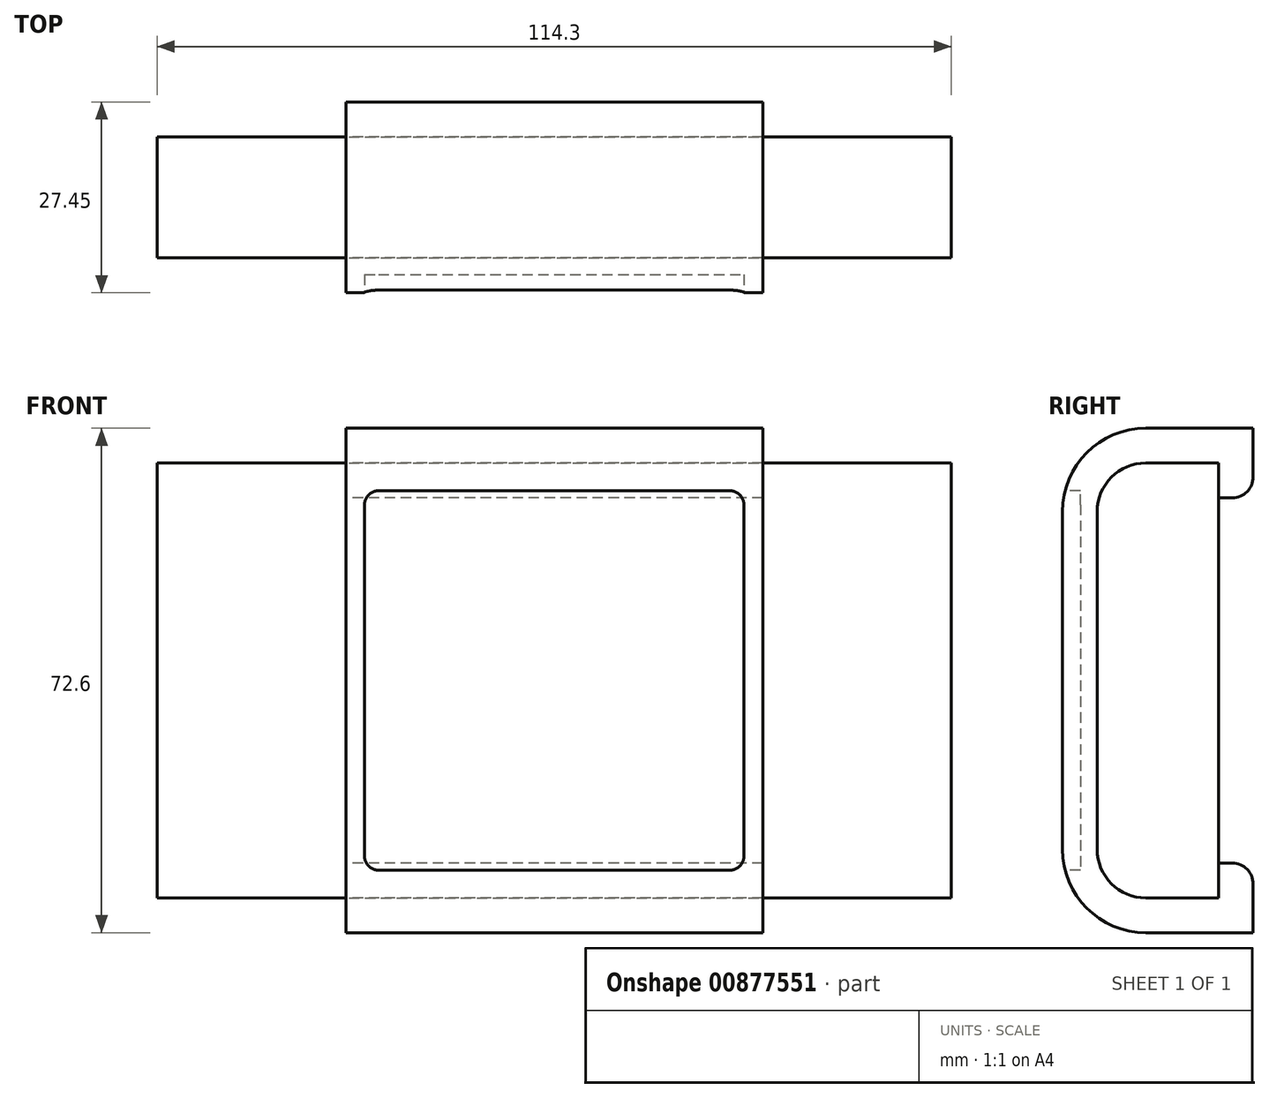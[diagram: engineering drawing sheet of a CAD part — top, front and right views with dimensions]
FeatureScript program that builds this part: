
annotation { "Feature Type Name" : "Feature", "Feature Type Description" : "" }
export const myFeature = defineFeature(function(context is Context, id is Id, definition is map)
    precondition{}
    {
        {
            var Q0;
            Q0=qCreatedBy(makeId("Front.planeOp"),FACE);
            var sketch = newSketch(context, id + "F0", { "sketchPlane" : qUnion([Q0])});
            skLineSegment(sketch, "E0.bottom", {"start": v(-57.15, 31.3) * mm, "end": v(57.15, 31.3) * mm});
            skLineSegment(sketch, "E0.top", {"start": v(-57.15, -31.3) * mm, "end": v(57.15, -31.3) * mm});
            skLineSegment(sketch, "E0.left", {"start": v(-57.15, 31.3) * mm, "end": v(-57.15, -31.3) * mm});
            skLineSegment(sketch, "E0.right", {"start": v(57.15, 31.3) * mm, "end": v(57.15, -31.3) * mm});
            skLineSegment(sketch, "E1", {"start": v(57.15, 31.3) * mm, "end": v(-57.15, -31.3) * mm, "construction": true});
            skLineSegment(sketch, "E2", {"start": v(-57.15, 31.3) * mm, "end": v(57.15, -31.3) * mm, "construction": true});
            skSolve(sketch);
        }
        {
            var Q0;
            Q0=makeQuery(id+"F0.imprint","IMPRINT",FACE,{"disambiguationData":[TD([[makeQuery(id+"F0.imprint","IMPRINT",EDGE,{"derivedFrom":sQuery(id+"F0.wireOp",EDGE,"E0.bottom")}),-1.0]])]});
            extrude(context, id + "F1", {"entities" : qUnion([Q0]), "depth" : 17.45 * mm, "offsetDistance" : 25 * mm});
        }
        {
            var Q0;
            Q0=makeQuery(id+"F1.opExtrude","CAP_EDGE",EDGE,{"disambiguationData":[OSD([sQuery(id+"F0.wireOp",EDGE,"E0.bottom")])],"isStart":false});
            var Q1;
            Q1=makeQuery(id+"F1.opExtrude","CAP_EDGE",EDGE,{"disambiguationData":[OSD([sQuery(id+"F0.wireOp",EDGE,"E0.top")])],"isStart":false});
            fillet(context, id + "F2", {"entities" : qUnion([Q0, Q1]), "radius" : 7 * mm, "tangentPropagation" : true, "allowEdgeOverflow" : false});
        }
        {
            var Q0;
            Q0=qCreatedBy(makeId("Right.planeOp"),FACE);
            var sketch = newSketch(context, id + "F3", { "sketchPlane" : qUnion([Q0])});
            skArc(sketch, "E3.0", {"start": v(-10.45, 36.3) * mm, "mid": v(-18.94, 32.79) * mm, "end": v(-22.45, 24.3) * mm});
            skArc(sketch, "E3.1", {"start": v(-22.45, -24.3) * mm, "mid": v(-18.94, -32.79) * mm, "end": v(-10.45, -36.3) * mm});
            skLineSegment(sketch, "E3.2", {"start": v(-10.45, -36.3) * mm, "end": v(5, -36.3) * mm});
            skLineSegment(sketch, "E3.3", {"start": v(-22.45, 24.3) * mm, "end": v(-22.45, -24.3) * mm});
            skLineSegment(sketch, "E3.4", {"start": v(5, -36.3) * mm, "end": v(5, -26.3) * mm});
            skLineSegment(sketch, "E3.5", {"start": v(5, 36.3) * mm, "end": v(-10.45, 36.3) * mm});
            skLineSegment(sketch, "E4", {"start": v(5, 26.3) * mm, "end": v(0, 26.3) * mm});
            skLineSegment(sketch, "E5", {"start": v(0, -26.3) * mm, "end": v(5, -26.3) * mm});
            skLineSegment(sketch, "E6.trimOffspring", {"start": v(5, 26.3) * mm, "end": v(5, 36.3) * mm});
            skLineSegment(sketch, "E7.0", {"start": v(0, -31.3) * mm, "end": v(0, -26.3) * mm});
            skLineSegment(sketch, "E7.1", {"start": v(-10.45, -31.3) * mm, "end": v(0, -31.3) * mm});
            skArc(sketch, "E7.2", {"start": v(-17.45, -24.3) * mm, "mid": v(-15.4, -29.25) * mm, "end": v(-10.45, -31.3) * mm});
            skLineSegment(sketch, "E7.3", {"start": v(0, 26.3) * mm, "end": v(0, 31.3) * mm});
            skLineSegment(sketch, "E7.4", {"start": v(0, 31.3) * mm, "end": v(-10.45, 31.3) * mm});
            skArc(sketch, "E7.5", {"start": v(-10.45, 31.3) * mm, "mid": v(-15.4, 29.25) * mm, "end": v(-17.45, 24.3) * mm});
            skLineSegment(sketch, "E7.6", {"start": v(-17.45, 24.3) * mm, "end": v(-17.45, -24.3) * mm});
            skSolve(sketch);
        }
        {
            var Q0;
            Q0=makeQuery(id+"F3.imprint","IMPRINT",FACE,{"disambiguationData":[TD([[makeQuery(id+"F3.imprint","IMPRINT",EDGE,{"derivedFrom":sQuery(id+"F3.wireOp",EDGE,"E3.0")}),1.0]])]});
            extrude(context, id + "F4", {"entities" : qUnion([Q0]), "endBound" : BoundingType.SYMMETRIC, "depth" : 60 * mm, "offsetDistance" : 25 * mm});
        }
        {
            var Q0;
            Q0=makeQuery(id+"F4.opExtrude","SWEPT_EDGE",EDGE,{"disambiguationData":[OSD([sQuery(id+"F3.wireOp",EDGE,"E4"),sQuery(id+"F3.wireOp",EDGE,"E6.trimOffspring")])]});
            var Q1;
            Q1=makeQuery(id+"F4.opExtrude","SWEPT_EDGE",EDGE,{"disambiguationData":[OSD([sQuery(id+"F3.wireOp",EDGE,"E3.4"),sQuery(id+"F3.wireOp",EDGE,"E5")])]});
            fillet(context, id + "F5", {"entities" : qUnion([Q0, Q1]), "radius" : 3 * mm, "tangentPropagation" : true, "allowEdgeOverflow" : false});
        }
        {
            var Q0;
            Q0=makeQuery(id+"F4.opExtrude","SWEPT_FACE",FACE,{"disambiguationData":[OSD([sQuery(id+"F3.wireOp",EDGE,"E3.3")])]});
            var sketch = newSketch(context, id + "F6", { "sketchPlane" : qUnion([Q0])});
            skLineSegment(sketch, "E8.bottom", {"start": v(-27.3, 27.3) * mm, "end": v(27.3, 27.3) * mm});
            skLineSegment(sketch, "E8.top", {"start": v(-27.3, -27.3) * mm, "end": v(27.3, -27.3) * mm});
            skLineSegment(sketch, "E8.left", {"start": v(-27.3, 27.3) * mm, "end": v(-27.3, -27.3) * mm});
            skLineSegment(sketch, "E8.right", {"start": v(27.3, 27.3) * mm, "end": v(27.3, -27.3) * mm});
            skPoint(sketch, "E8.middle", {"position": v(0, 0) * mm});
            skSolve(sketch);
        }
        {
            var Q0;
            {var subQ0=sQuery(id+"F6.wireOp",EDGE,"E8.bottom");Q0=makeQuery(id+"F6.imprint","IMPRINT",FACE,{"disambiguationData":[TD([[makeQuery(id+"F6.imprint","IMPRINT",EDGE,{"derivedFrom":subQ0}),-1.0]])]});}
            var Q1;
            {var subQ0=sQuery(id+"F6.wireOp",EDGE,"E8.top");Q1=makeQuery(id+"F6.imprint","IMPRINT",FACE,{"disambiguationData":[TD([[makeQuery(id+"F6.imprint","IMPRINT",EDGE,{"derivedFrom":subQ0}),1.0]])]});}
            var Q2;
            {var subQ0=sQuery(id+"F6.wireOp",EDGE,"E8.left");var subQ1=sQuery(id+"F3.wireOp",EDGE,"E3.3");var subQ2=makeQuery(id+"F4.opExtrude","SWEPT_EDGE",EDGE,{"disambiguationData":[OSD([sQuery(id+"F3.wireOp",EDGE,"E3.0"),subQ1])]});var subQ3=makeQuery(id+"F6.imprint","INTERSECT",VERTEX,{"derivedFrom":[subQ2,subQ0]});Q2=makeQuery(id+"F6.imprint","IMPRINT",FACE,{"disambiguationData":[TD([[makeQuery(id+"F6.imprint","IMPRINT",EDGE,{"disambiguationData":[TD([[subQ3,-1.0]])],"derivedFrom":subQ0}),1.0]])]});}
            extrude(context, id + "F7", {"entities" : qUnion([Q0, Q1, Q2]), "operationType" : NewBodyOperationType.REMOVE, "oppositeDirection" : true, "depth" : 2.6 * mm, "offsetDistance" : 25 * mm});
        }
        {
            var Q0;
            Q0=makeQuery(id+"F7.boolean.opBoolean","COPY",EDGE,{"derivedFrom":makeQuery(id+"F7.opExtrude","SWEPT_EDGE",EDGE,{"disambiguationData":[OSD([sQuery(id+"F6.wireOp",EDGE,"E8.bottom"),sQuery(id+"F6.wireOp",EDGE,"E8.left")])]})});
            var Q1;
            Q1=makeQuery(id+"F7.boolean.opBoolean","COPY",EDGE,{"derivedFrom":makeQuery(id+"F7.opExtrude","SWEPT_EDGE",EDGE,{"disambiguationData":[OSD([sQuery(id+"F6.wireOp",EDGE,"E8.bottom"),sQuery(id+"F6.wireOp",EDGE,"E8.right")])]})});
            var Q2;
            Q2=makeQuery(id+"F7.boolean.opBoolean","COPY",EDGE,{"derivedFrom":makeQuery(id+"F7.opExtrude","SWEPT_EDGE",EDGE,{"disambiguationData":[OSD([sQuery(id+"F6.wireOp",EDGE,"E8.top"),sQuery(id+"F6.wireOp",EDGE,"E8.right")])]})});
            var Q3;
            Q3=makeQuery(id+"F7.boolean.opBoolean","COPY",EDGE,{"derivedFrom":makeQuery(id+"F7.opExtrude","SWEPT_EDGE",EDGE,{"disambiguationData":[OSD([sQuery(id+"F6.wireOp",EDGE,"E8.top"),sQuery(id+"F6.wireOp",EDGE,"E8.left")])]})});
            fillet(context, id + "F8", {"entities" : qUnion([Q0, Q1, Q2, Q3]), "radius" : 2 * mm, "tangentPropagation" : true, "allowEdgeOverflow" : false});
        }
    });
